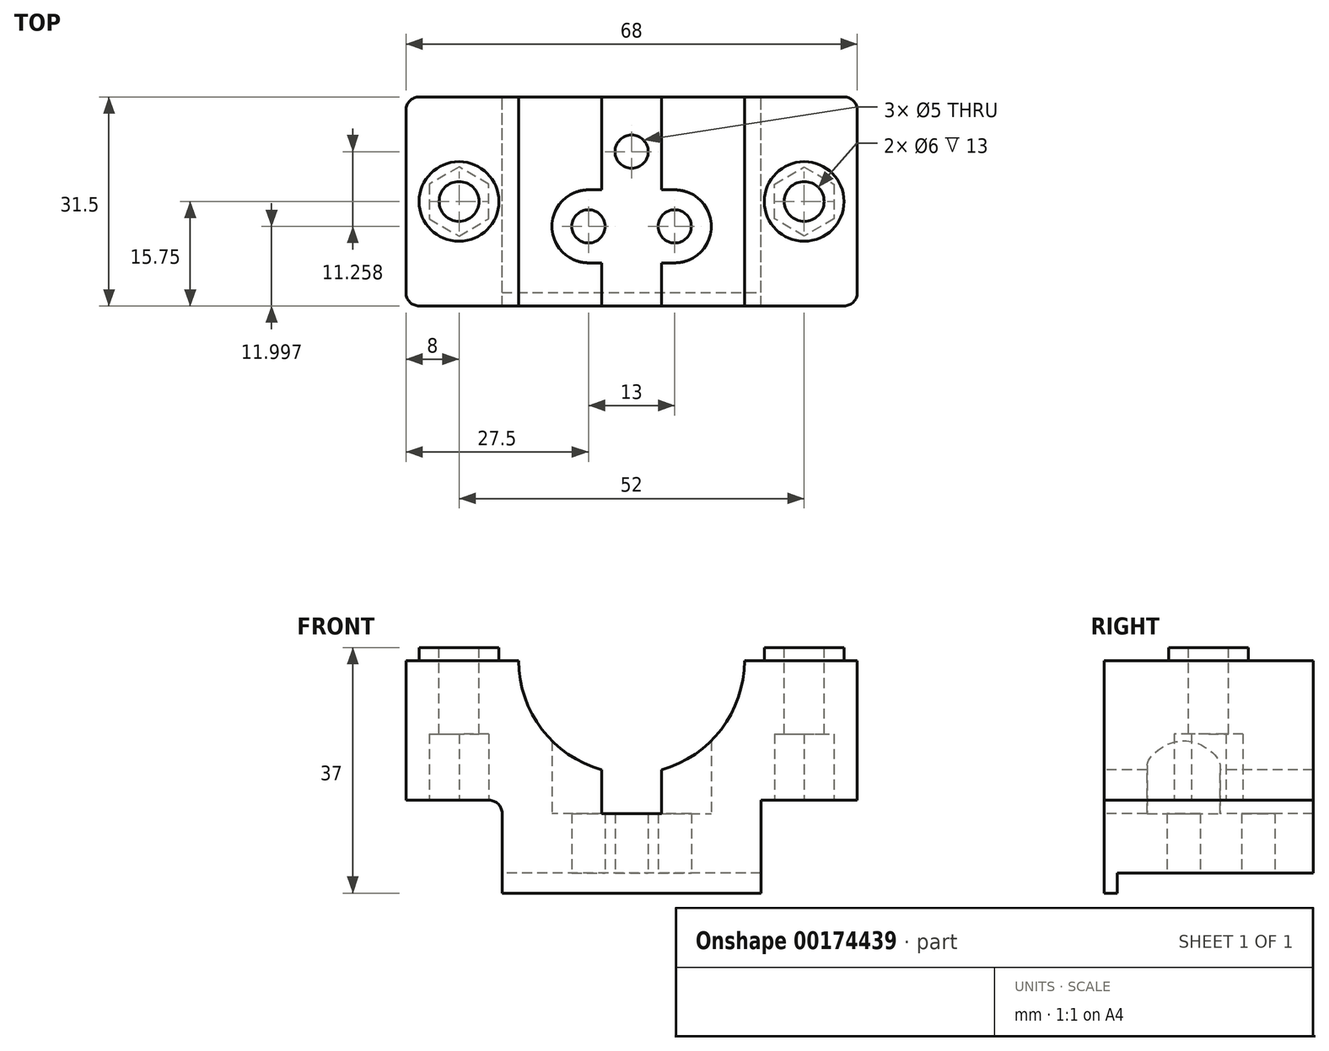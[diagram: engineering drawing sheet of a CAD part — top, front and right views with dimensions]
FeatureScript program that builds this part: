
annotation { "Feature Type Name" : "Feature", "Feature Type Description" : "" }
export const myFeature = defineFeature(function(context is Context, id is Id, definition is map)
    precondition{}
    {
        {
            var Q0;
            Q0=qCreatedBy(makeId("Top.planeOp"),FACE);
            var sketch = newSketch(context, id + "F0", { "sketchPlane" : qUnion([Q0])});
            skLineSegment(sketch, "E0.bottom", {"start": v(34, -15.75) * mm, "end": v(-34, -15.75) * mm});
            skLineSegment(sketch, "E0.top", {"start": v(34, 15.75) * mm, "end": v(-34, 15.75) * mm});
            skLineSegment(sketch, "E0.left", {"start": v(34, -15.75) * mm, "end": v(34, 15.75) * mm});
            skLineSegment(sketch, "E0.right", {"start": v(-34, -15.75) * mm, "end": v(-34, 15.75) * mm});
            skPoint(sketch, "E0.middle", {"position": v(0, 0) * mm});
            skSolve(sketch);
        }
        {
            var Q0;
            Q0=qSketchRegion(id+"F0",true);
            extrude(context, id + "F1", {"entities" : qUnion([Q0]), "oppositeDirection" : true, "depth" : 21 * mm});
        }
        {
            var Q0;
            Q0=makeQuery(id+"F1.opExtrude","CAP_FACE",FACE,{"disambiguationData":[OSD([sQuery(id+"F0.wireOp",EDGE,"E0.bottom"),sQuery(id+"F0.wireOp",EDGE,"E0.top"),sQuery(id+"F0.wireOp",EDGE,"E0.left"),sQuery(id+"F0.wireOp",EDGE,"E0.right")])],"isStart":false});
            var sketch = newSketch(context, id + "F2", { "sketchPlane" : qUnion([Q0])});
            skLineSegment(sketch, "E1.bottom", {"start": v(19.5, 15.75) * mm, "end": v(-19.5, 15.75) * mm});
            skLineSegment(sketch, "E1.top", {"start": v(19.5, -15.75) * mm, "end": v(-19.5, -15.75) * mm});
            skLineSegment(sketch, "E1.left", {"start": v(19.5, 15.75) * mm, "end": v(19.5, -15.75) * mm});
            skLineSegment(sketch, "E1.right", {"start": v(-19.5, 15.75) * mm, "end": v(-19.5, -15.75) * mm});
            skPoint(sketch, "E1.middle", {"position": v(0, 0) * mm});
            skSolve(sketch);
        }
        {
            var Q0;
            Q0=qSketchRegion(id+"F2",true);
            extrude(context, id + "F3", {"entities" : qUnion([Q0]), "operationType" : NewBodyOperationType.ADD, "depth" : 11 * mm});
        }
        {
            var Q0;
            Q0=makeQuery(id+"F1.opExtrude","CAP_FACE",FACE,{"disambiguationData":[OSD([sQuery(id+"F0.wireOp",EDGE,"E0.bottom"),sQuery(id+"F0.wireOp",EDGE,"E0.top"),sQuery(id+"F0.wireOp",EDGE,"E0.left"),sQuery(id+"F0.wireOp",EDGE,"E0.right")])],"isStart":true});
            var sketch = newSketch(context, id + "F4", { "sketchPlane" : qUnion([Q0])});
            skLineSegment(sketch, "E2", {"start": v(-34, 0) * mm, "end": v(0, 0) * mm, "construction": true});
            skLineSegment(sketch, "E3", {"start": v(0, 0) * mm, "end": v(0, 15.75) * mm, "construction": true});
            skCircle(sketch, "E4", {"center": v(-26, 0) * mm, "radius": 6 * mm});
            skCircle(sketch, "E5.MirrorC", {"center": v(26, 0) * mm, "radius": 6 * mm});
            skSolve(sketch);
        }
        {
            var Q0;
            Q0=qSketchRegion(id+"F4",true);
            extrude(context, id + "F5", {"entities" : qUnion([Q0]), "operationType" : NewBodyOperationType.ADD, "depth" : 2 * mm});
        }
        {
            var Q0;
            Q0=makeQuery(id+"F5.opExtrude","CAP_FACE",FACE,{"disambiguationData":[OSD([sQuery(id+"F4.wireOp",EDGE,"E4")])],"isStart":false});
            var sketch = newSketch(context, id + "F6", { "sketchPlane" : qUnion([Q0])});
            skCircle(sketch, "E6", {"center": v(-26, 0) * mm, "radius": 3 * mm});
            skLineSegment(sketch, "E7", {"start": v(-26, 0) * mm, "end": v(26, 0) * mm, "construction": true});
            skLineSegment(sketch, "E8", {"start": v(0, 0) * mm, "end": v(0, 15.75) * mm, "construction": true});
            skCircle(sketch, "E9.MirrorC", {"center": v(26, 0) * mm, "radius": 3 * mm});
            skSolve(sketch);
        }
        {
            var Q0;
            Q0=qSketchRegion(id+"F6",true);
            extrude(context, id + "F7", {"entities" : qUnion([Q0]), "operationType" : NewBodyOperationType.REMOVE, "endBound" : BoundingType.THROUGH_ALL, "oppositeDirection" : true, "depth" : 25 * mm});
        }
        {
            var Q0;
            {var subQ0=sQuery(id+"F0.wireOp",EDGE,"E0.right");var subQ1=sQuery(id+"F0.wireOp",EDGE,"E0.top");var subQ2=sQuery(id+"F0.wireOp",EDGE,"E0.bottom");Q0=makeQuery(id+"F3.boolean.opBoolean","SPLIT",FACE,{"disambiguationData":[TD([makeQuery(id+"F1.opExtrude","SWEPT_FACE",FACE,{"disambiguationData":[OSD([subQ0])]})])],"derivedFrom":makeQuery(id+"F1.opExtrude","CAP_FACE",FACE,{"disambiguationData":[OSD([subQ2,subQ1,sQuery(id+"F0.wireOp",EDGE,"E0.left"),subQ0])],"isStart":false})});}
            var sketch = newSketch(context, id + "F8", { "sketchPlane" : qUnion([Q0])});
            skCircle(sketch, "E10.cCircle", {"center": v(-26, 0) * mm, "radius": 4.5 * mm, "construction": true});
            skLineSegment(sketch, "E10.0", {"start": v(-30.5, 2.6) * mm, "end": v(-26, 5.2) * mm});
            skLineSegment(sketch, "E10.1", {"start": v(-26, 5.2) * mm, "end": v(-21.5, 2.6) * mm});
            skLineSegment(sketch, "E10.2", {"start": v(-21.5, 2.6) * mm, "end": v(-21.5, -2.6) * mm});
            skLineSegment(sketch, "E10.3", {"start": v(-21.5, -2.6) * mm, "end": v(-26, -5.2) * mm});
            skLineSegment(sketch, "E10.4", {"start": v(-26, -5.2) * mm, "end": v(-30.5, -2.6) * mm});
            skLineSegment(sketch, "E10.5", {"start": v(-30.5, -2.6) * mm, "end": v(-30.5, 2.6) * mm});
            skPoint(sketch, "E10.0.midPoint", {"position": v(-28.25, 3.9) * mm});
            skLineSegment(sketch, "E11", {"start": v(-26, 0) * mm, "end": v(-26, 5.2) * mm, "construction": true});
            skLineSegment(sketch, "E12", {"start": v(-26, 0) * mm, "end": v(0, 0) * mm, "construction": true});
            skLineSegment(sketch, "E13", {"start": v(0, 0) * mm, "end": v(0, 15.75) * mm, "construction": true});
            skLineSegment(sketch, "E14.MirrorCS", {"start": v(30.5, -2.6) * mm, "end": v(30.5, 2.6) * mm});
            skLineSegment(sketch, "E15.MirrorCS", {"start": v(21.5, -2.6) * mm, "end": v(26, -5.2) * mm});
            skLineSegment(sketch, "E16.MirrorCS", {"start": v(21.5, 2.6) * mm, "end": v(21.5, -2.6) * mm});
            skLineSegment(sketch, "E17.MirrorCS", {"start": v(30.5, 2.6) * mm, "end": v(26, 5.2) * mm});
            skLineSegment(sketch, "E18.MirrorCS", {"start": v(26, 0) * mm, "end": v(26, 5.2) * mm, "construction": true});
            skLineSegment(sketch, "E19.MirrorCS", {"start": v(26, 0) * mm, "end": v(0, 0) * mm, "construction": true});
            skLineSegment(sketch, "E20.MirrorCS", {"start": v(26, -5.2) * mm, "end": v(30.5, -2.6) * mm});
            skLineSegment(sketch, "E21.MirrorCS", {"start": v(26, 5.2) * mm, "end": v(21.5, 2.6) * mm});
            skPoint(sketch, "E22.MirrorP", {"position": v(28.25, 3.9) * mm});
            skCircle(sketch, "E23.MirrorC", {"center": v(26, 0) * mm, "radius": 4.5 * mm, "construction": true});
            skSolve(sketch);
        }
        {
            var Q0;
            Q0=qSketchRegion(id+"F8",true);
            extrude(context, id + "F9", {"entities" : qUnion([Q0]), "operationType" : NewBodyOperationType.REMOVE, "oppositeDirection" : true, "depth" : 10 * mm});
        }
        {
            var Q0;
            Q0=makeQuery(id+"F3.boolean.opBoolean","MERGE",FACE,{"derivedFrom":[makeQuery(id+"F1.opExtrude","SWEPT_FACE",FACE,{"disambiguationData":[OSD([sQuery(id+"F0.wireOp",EDGE,"E0.bottom")])]}),makeQuery(id+"F3.opExtrude","SWEPT_FACE",FACE,{"disambiguationData":[OSD([sQuery(id+"F2.wireOp",EDGE,"E1.bottom")])]})]});
            var sketch = newSketch(context, id + "F10", { "sketchPlane" : qUnion([Q0])});
            skArc(sketch, "E24", {"start": v(4.5, -16.4) * mm, "mid": v(13.52, -10.3) * mm, "end": v(17, 0) * mm});
            skLineSegment(sketch, "E25.bottom", {"start": v(-4.5, -23) * mm, "end": v(4.5, -23) * mm});
            skLineSegment(sketch, "E25.left", {"start": v(-4.5, -23) * mm, "end": v(-4.5, -16.4) * mm});
            skLineSegment(sketch, "E25.right", {"start": v(4.5, -23) * mm, "end": v(4.5, -16.4) * mm});
            skPoint(sketch, "E25.middle", {"position": v(0, -17) * mm});
            skLineSegment(sketch, "E26", {"start": v(-17, 0) * mm, "end": v(17, 0) * mm});
            skPoint(sketch, "E25.top.start.orphan", {"position": v(-4.5, -11) * mm});
            skPoint(sketch, "E27.orphan", {"position": v(4.5, -11) * mm});
            skArc(sketch, "E28.trimOffspring", {"start": v(-17, 0) * mm, "mid": v(-13.52, -10.3) * mm, "end": v(-4.5, -16.4) * mm});
            skLineSegment(sketch, "E29", {"start": v(0, 0) * mm, "end": v(0, -23) * mm, "construction": true});
            skSolve(sketch);
        }
        {
            var Q0;
            Q0=qSketchRegion(id+"F10",true);
            extrude(context, id + "F11", {"entities" : qUnion([Q0]), "operationType" : NewBodyOperationType.REMOVE, "endBound" : BoundingType.THROUGH_ALL, "oppositeDirection" : true, "depth" : 25 * mm});
        }
        {
            var Q0;
            Q0=makeQuery(id+"F3.opExtrude","CAP_FACE",FACE,{"disambiguationData":[OSD([sQuery(id+"F2.wireOp",EDGE,"E1.bottom"),sQuery(id+"F2.wireOp",EDGE,"E1.top"),sQuery(id+"F2.wireOp",EDGE,"E1.left"),sQuery(id+"F2.wireOp",EDGE,"E1.right")])],"isStart":false});
            var sketch = newSketch(context, id + "F12", { "sketchPlane" : qUnion([Q0])});
            skLineSegment(sketch, "E30.bottom", {"start": v(-19.5, 15.75) * mm, "end": v(19.5, 15.75) * mm});
            skLineSegment(sketch, "E30.top", {"start": v(-19.5, 13.75) * mm, "end": v(19.5, 13.75) * mm});
            skLineSegment(sketch, "E30.left", {"start": v(-19.5, 15.75) * mm, "end": v(-19.5, 13.75) * mm});
            skLineSegment(sketch, "E30.right", {"start": v(19.5, 15.75) * mm, "end": v(19.5, 13.75) * mm});
            skLineSegment(sketch, "E31", {"start": v(-19.5, 0) * mm, "end": v(0, 0) * mm, "construction": true});
            skLineSegment(sketch, "E32", {"start": v(0, 0) * mm, "end": v(0, 15.75) * mm, "construction": true});
            skLineSegment(sketch, "E33.MirrorCS", {"start": v(19.5, -15.75) * mm, "end": v(19.5, -13.75) * mm, "construction": true});
            skLineSegment(sketch, "E34.MirrorCS", {"start": v(-19.5, -15.75) * mm, "end": v(-19.5, -13.75) * mm, "construction": true});
            skLineSegment(sketch, "E35.MirrorCS", {"start": v(-19.5, -13.75) * mm, "end": v(19.5, -13.75) * mm, "construction": true});
            skLineSegment(sketch, "E36.MirrorCS", {"start": v(-19.5, -15.75) * mm, "end": v(19.5, -15.75) * mm});
            skSolve(sketch);
        }
        {
            var Q0;
            Q0=makeQuery(id+"F12.imprint","IMPRINT",FACE,{"disambiguationData":[TD([[makeQuery(id+"F12.imprint","IMPRINT",EDGE,{"derivedFrom":sQuery(id+"F12.wireOp",EDGE,"E30.bottom")}),1.0]])]});
            var Q1;
            Q1=makeQuery(id+"F12.imprint","IMPRINT",FACE,{"disambiguationData":[TD([[makeQuery(id+"F12.imprint","IMPRINT",EDGE,{"derivedFrom":sQuery(id+"F12.wireOp",EDGE,"E33.MirrorCS")}),-1.0]])]});
            extrude(context, id + "F13", {"entities" : qUnion([Q0, Q1]), "operationType" : NewBodyOperationType.ADD, "depth" : 3 * mm});
        }
        {
            var Q0;
            Q0=makeQuery(id+"F3.opExtrude","CAP_FACE",FACE,{"disambiguationData":[OSD([sQuery(id+"F2.wireOp",EDGE,"E1.bottom"),sQuery(id+"F2.wireOp",EDGE,"E1.top"),sQuery(id+"F2.wireOp",EDGE,"E1.left"),sQuery(id+"F2.wireOp",EDGE,"E1.right")])],"isStart":false});
            var sketch = newSketch(context, id + "F14", { "sketchPlane" : qUnion([Q0])});
            skCircle(sketch, "E37.cCircle", {"center": v(0, 0) * mm, "radius": 3.75 * mm, "construction": true});
            skLineSegment(sketch, "E37.0", {"start": v(-6.5, 3.75) * mm, "end": v(6.5, 3.75) * mm, "construction": true});
            skLineSegment(sketch, "E37.1", {"start": v(6.5, 3.75) * mm, "end": v(0, -7.5) * mm, "construction": true});
            skLineSegment(sketch, "E37.2", {"start": v(0, -7.5) * mm, "end": v(-6.5, 3.75) * mm, "construction": true});
            skPoint(sketch, "E37.0.midPoint", {"position": v(0, 3.75) * mm});
            skCircle(sketch, "E38", {"center": v(-6.5, 3.75) * mm, "radius": 2.5 * mm});
            skCircle(sketch, "E39", {"center": v(6.5, 3.75) * mm, "radius": 2.5 * mm});
            skCircle(sketch, "E40", {"center": v(0, -7.5) * mm, "radius": 2.5 * mm});
            skLineSegment(sketch, "E41.top", {"start": v(-4, 3.75) * mm, "end": v(4, 3.75) * mm, "construction": true});
            skSolve(sketch);
        }
        {
            var Q0;
            Q0=makeQuery(id+"F14.imprint","IMPRINT",FACE,{"disambiguationData":[TD([[makeQuery(id+"F14.imprint","IMPRINT",EDGE,{"derivedFrom":sQuery(id+"F14.wireOp",EDGE,"E38")}),1.0]])]});
            var Q1;
            Q1=makeQuery(id+"F14.imprint","IMPRINT",FACE,{"disambiguationData":[TD([[makeQuery(id+"F14.imprint","IMPRINT",EDGE,{"derivedFrom":sQuery(id+"F14.wireOp",EDGE,"E39")}),1.0]])]});
            var Q2;
            Q2=makeQuery(id+"F14.imprint","IMPRINT",FACE,{"disambiguationData":[TD([[makeQuery(id+"F14.imprint","IMPRINT",EDGE,{"derivedFrom":sQuery(id+"F14.wireOp",EDGE,"E40")}),1.0]])]});
            extrude(context, id + "F15", {"entities" : qUnion([Q0, Q1, Q2]), "operationType" : NewBodyOperationType.REMOVE, "endBound" : BoundingType.THROUGH_ALL, "oppositeDirection" : true, "depth" : 25 * mm});
        }
        {
            var Q0;
            Q0=makeQuery(id+"F11.boolean.opBoolean","COPY",FACE,{"derivedFrom":makeQuery(id+"F11.opExtrude","SWEPT_FACE",FACE,{"disambiguationData":[OSD([sQuery(id+"F10.wireOp",EDGE,"E25.bottom")])]})});
            var sketch = newSketch(context, id + "F16", { "sketchPlane" : qUnion([Q0])});
            skLineSegment(sketch, "E42", {"start": v(-6.5, -3.75) * mm, "end": v(6.5, -3.75) * mm, "construction": true});
            skArc(sketch, "E43.0.startCap", {"start": v(-6.5, -9.25) * mm, "mid": v(-12, -3.75) * mm, "end": v(-6.5, 1.75) * mm});
            skArc(sketch, "E43.0.endCap", {"start": v(6.5, 1.75) * mm, "mid": v(12, -3.75) * mm, "end": v(6.5, -9.25) * mm});
            skLineSegment(sketch, "E43.0.left", {"start": v(-6.5, 1.75) * mm, "end": v(6.5, 1.75) * mm});
            skLineSegment(sketch, "E43.0.right", {"start": v(-6.5, -9.25) * mm, "end": v(6.5, -9.25) * mm});
            skSolve(sketch);
        }
        {
            var Q0;
            Q0=qSketchRegion(id+"F16",true);
            extrude(context, id + "F17", {"entities" : qUnion([Q0]), "operationType" : NewBodyOperationType.REMOVE, "endBound" : BoundingType.THROUGH_ALL, "depth" : 25 * mm});
        }
        {
            var Q0;
            Q0=makeQuery(id+"F1.opExtrude","SWEPT_EDGE",EDGE,{"disambiguationData":[OSD([sQuery(id+"F0.wireOp",EDGE,"E0.bottom"),sQuery(id+"F0.wireOp",EDGE,"E0.right")])]});
            var Q1;
            Q1=makeQuery(id+"F1.opExtrude","SWEPT_EDGE",EDGE,{"disambiguationData":[OSD([sQuery(id+"F0.wireOp",EDGE,"E0.bottom"),sQuery(id+"F0.wireOp",EDGE,"E0.left")])]});
            var Q2;
            Q2=makeQuery(id+"F1.opExtrude","SWEPT_EDGE",EDGE,{"disambiguationData":[OSD([sQuery(id+"F0.wireOp",EDGE,"E0.top"),sQuery(id+"F0.wireOp",EDGE,"E0.left")])]});
            var Q3;
            Q3=makeQuery(id+"F1.opExtrude","SWEPT_EDGE",EDGE,{"disambiguationData":[OSD([sQuery(id+"F0.wireOp",EDGE,"E0.top"),sQuery(id+"F0.wireOp",EDGE,"E0.right")])]});
            fillet(context, id + "F18", {"entities" : qUnion([Q0, Q1, Q2, Q3]), "radius" : 2 * mm, "tangentPropagation" : true, "allowEdgeOverflow" : false});
        }
        {
            var Q0;
            Q0=makeQuery(id+"F3.opExtrude","CAP_EDGE",EDGE,{"disambiguationData":[OSD([sQuery(id+"F2.wireOp",EDGE,"E1.right")])],"isStart":true});
            var Q1;
            Q1=makeQuery(id+"F3.opExtrude","CAP_EDGE",EDGE,{"disambiguationData":[OSD([sQuery(id+"F2.wireOp",EDGE,"E1.left")])],"isStart":true});
            fillet(context, id + "F19", {"entities" : qUnion([Q0, Q1]), "radius" : 2 * mm, "tangentPropagation" : true, "allowEdgeOverflow" : false});
        }
    });
